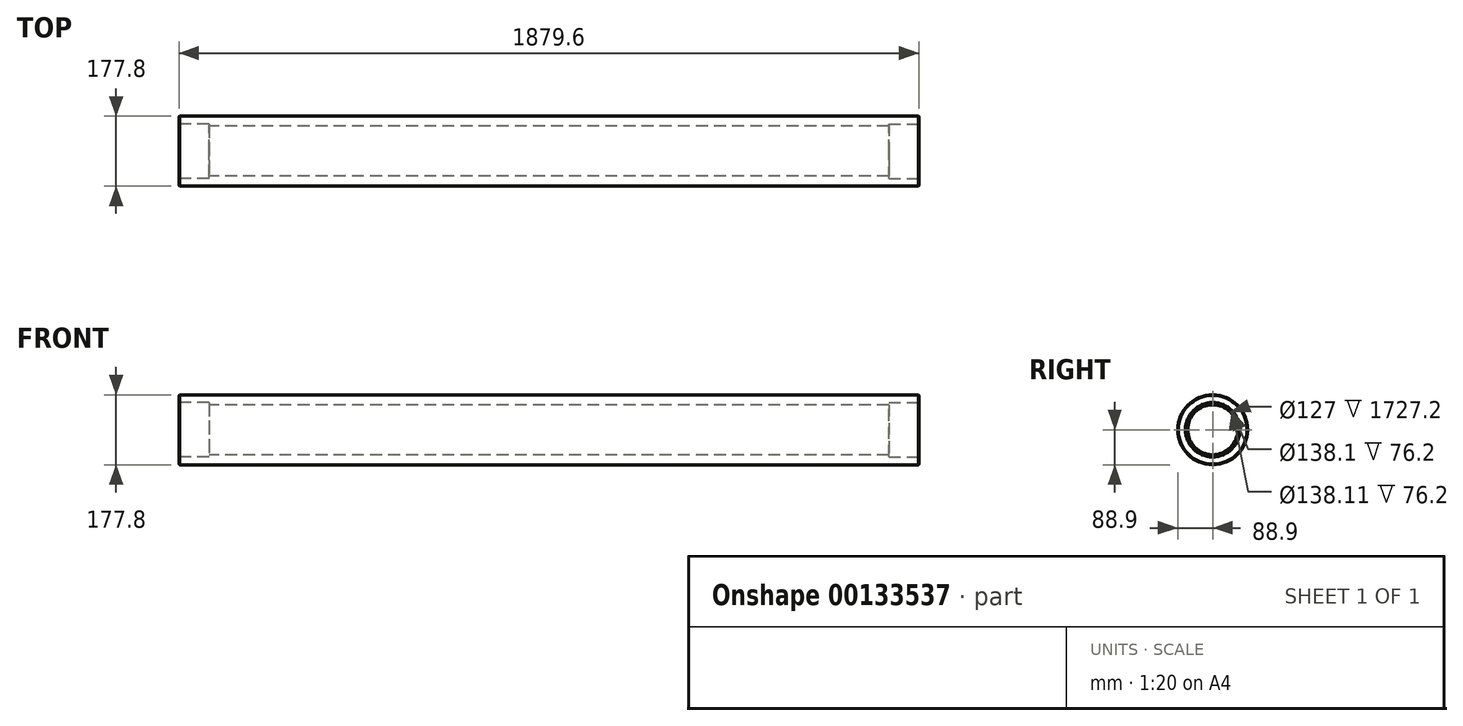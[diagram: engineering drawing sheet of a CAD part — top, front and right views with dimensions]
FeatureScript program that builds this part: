
annotation { "Feature Type Name" : "Feature", "Feature Type Description" : "" }
export const myFeature = defineFeature(function(context is Context, id is Id, definition is map)
    precondition{}
    {
        {
            var Q0;
            Q0=qCreatedBy(makeId("Right.planeOp"),FACE);
            var sketch = newSketch(context, id + "F0", { "sketchPlane" : qUnion([Q0])});
            skCircle(sketch, "E0", {"center": v(0, 0) * mm, "radius": 88.9 * mm});
            skCircle(sketch, "E1", {"center": v(0, 0) * mm, "radius": 63.5 * mm});
            skSolve(sketch);
        }
        {
            var Q0;
            Q0 = qSketchRegion(id + "F0", true);
            extrude(context, id + "F1", {"entities" : qUnion([Q0]), "endBound" : BoundingType.SYMMETRIC, "depth" : 1879.6 * mm});
        }
        {
            var Q0;
            Q0=makeQuery(id+"F1.opExtrude","CAP_FACE",FACE,{"disambiguationData":[OSD([sQuery(id+"F0.wireOp",EDGE,"E0"),sQuery(id+"F0.wireOp",EDGE,"E1")])],"isStart":false});
            var sketch = newSketch(context, id + "F2", { "sketchPlane" : qUnion([Q0])});
            skCircle(sketch, "E2", {"center": v(0, 0) * mm, "radius": 69.05 * mm});
            skSolve(sketch);
        }
        {
            var Q0;
            Q0=makeQuery(id+"F2.imprint","IMPRINT",FACE,{"disambiguationData":[TD([[makeQuery(id+"F2.imprint","IMPRINT",EDGE,{"derivedFrom":sQuery(id+"F2.wireOp",EDGE,"E2")}),1.0]])]});
            extrude(context, id + "F3", {"entities" : qUnion([Q0]), "operationType" : NewBodyOperationType.REMOVE, "oppositeDirection" : true, "depth" : 76.2 * mm});
        }
        {
            var Q0;
            Q0=makeQuery(id+"F1.opExtrude","CAP_FACE",FACE,{"disambiguationData":[OSD([sQuery(id+"F0.wireOp",EDGE,"E0"),sQuery(id+"F0.wireOp",EDGE,"E1")])],"isStart":true});
            var sketch = newSketch(context, id + "F4", { "sketchPlane" : qUnion([Q0])});
            skCircle(sketch, "E3", {"center": v(0, 0) * mm, "radius": 69.06 * mm});
            skSolve(sketch);
        }
        {
            var Q0;
            Q0 = qSketchRegion(id + "F4", true);
            extrude(context, id + "F5", {"entities" : qUnion([Q0]), "operationType" : NewBodyOperationType.REMOVE, "oppositeDirection" : true, "depth" : 76.2 * mm});
        }
        {
            var Q0;
            Q0=makeQuery(id+"F1.opExtrude","CAP_EDGE",EDGE,{"disambiguationData":[OSD([sQuery(id+"F0.wireOp",EDGE,"E0")])],"isStart":true});
            var Q1;
            Q1=makeQuery(id+"F1.opExtrude","CAP_EDGE",EDGE,{"disambiguationData":[OSD([sQuery(id+"F0.wireOp",EDGE,"E0")])],"isStart":false});
            chamfer(context, id + "F6", {"entities" : qUnion([Q0, Q1]), "width" : 1.52 * mm, "tangentPropagation" : true});
        }
    });
